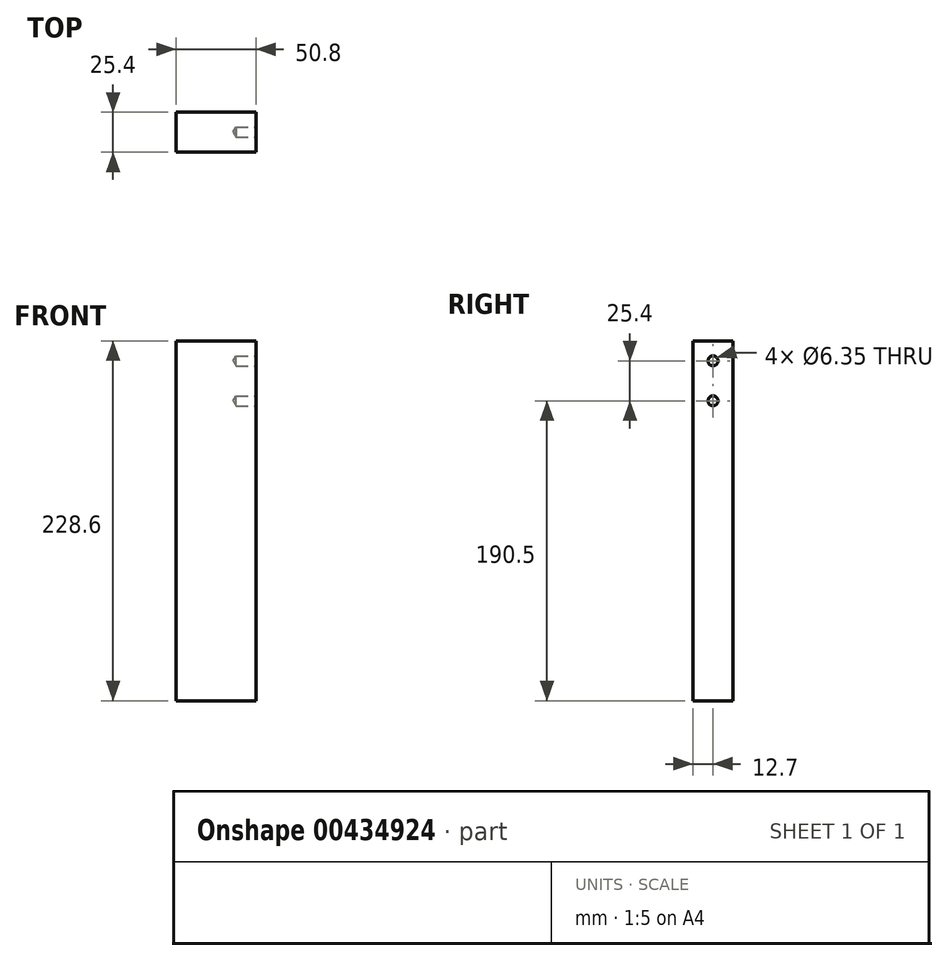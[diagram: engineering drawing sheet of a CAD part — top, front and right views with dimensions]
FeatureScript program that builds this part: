
annotation { "Feature Type Name" : "Feature", "Feature Type Description" : "" }
export const myFeature = defineFeature(function(context is Context, id is Id, definition is map)
    precondition{}
    {
        {
            var Q0;
            Q0=qCreatedBy(makeId("Front.planeOp"),FACE);
            var sketch = newSketch(context, id + "F0", { "sketchPlane" : qUnion([Q0])});
            skLineSegment(sketch, "E0.bottom", {"start": v(0, 0) * mm, "end": v(50.8, 0) * mm});
            skLineSegment(sketch, "E0.top", {"start": v(0, 228.6) * mm, "end": v(50.8, 228.6) * mm});
            skLineSegment(sketch, "E0.left", {"start": v(0, 0) * mm, "end": v(0, 228.6) * mm});
            skLineSegment(sketch, "E0.right", {"start": v(50.8, 0) * mm, "end": v(50.8, 228.6) * mm});
            skSolve(sketch);
        }
        {
            var Q0;
            Q0 = qSketchRegion(id + "F0", true);
            extrude(context, id + "F1", {"entities" : qUnion([Q0]), "depth" : 25.4 * mm});
        }
        {
            var Q0;
            Q0=makeQuery(id+"F1.opExtrude","SWEPT_FACE",FACE,{"disambiguationData":[OSD([sQuery(id+"F0.wireOp",EDGE,"E0.right")])]});
            var sketch = newSketch(context, id + "F2", { "sketchPlane" : qUnion([Q0])});
            skPoint(sketch, "E1", {"position": v(-12.7, 215.9) * mm});
            skPoint(sketch, "E2", {"position": v(-12.7, 190.5) * mm});
            skSolve(sketch);
        }
        {
            var Q0;
            Q0=sQuery(id+"F2.wireOp",VERTEX,"E1");
            var Q1;
            Q1=sQuery(id+"F2.wireOp",VERTEX,"E2");
            var Q2;
            Q2=makeQuery(id+"F1.opExtrude","SWEPT_BODY",BODY,{"disambiguationData":[OSD([sQuery(id+"F0.wireOp",EDGE,"E0.bottom"),sQuery(id+"F0.wireOp",EDGE,"E0.top"),sQuery(id+"F0.wireOp",EDGE,"E0.left"),sQuery(id+"F0.wireOp",EDGE,"E0.right")])]});
            hole(context, id + "F3", {"style" : HoleStyle.SIMPLE, "endStyle" : HoleEndStyle.BLIND, "holeDiameter" : 6.35 * mm, "holeDepth" : 12.7 * mm, "isTappedThrough" : true, "tappedDepth" : 12.7 * mm, "tapClearance" : 3, "locations" : qUnion([Q0, Q1]), "scope" : qUnion([Q2])});
        }
    });
